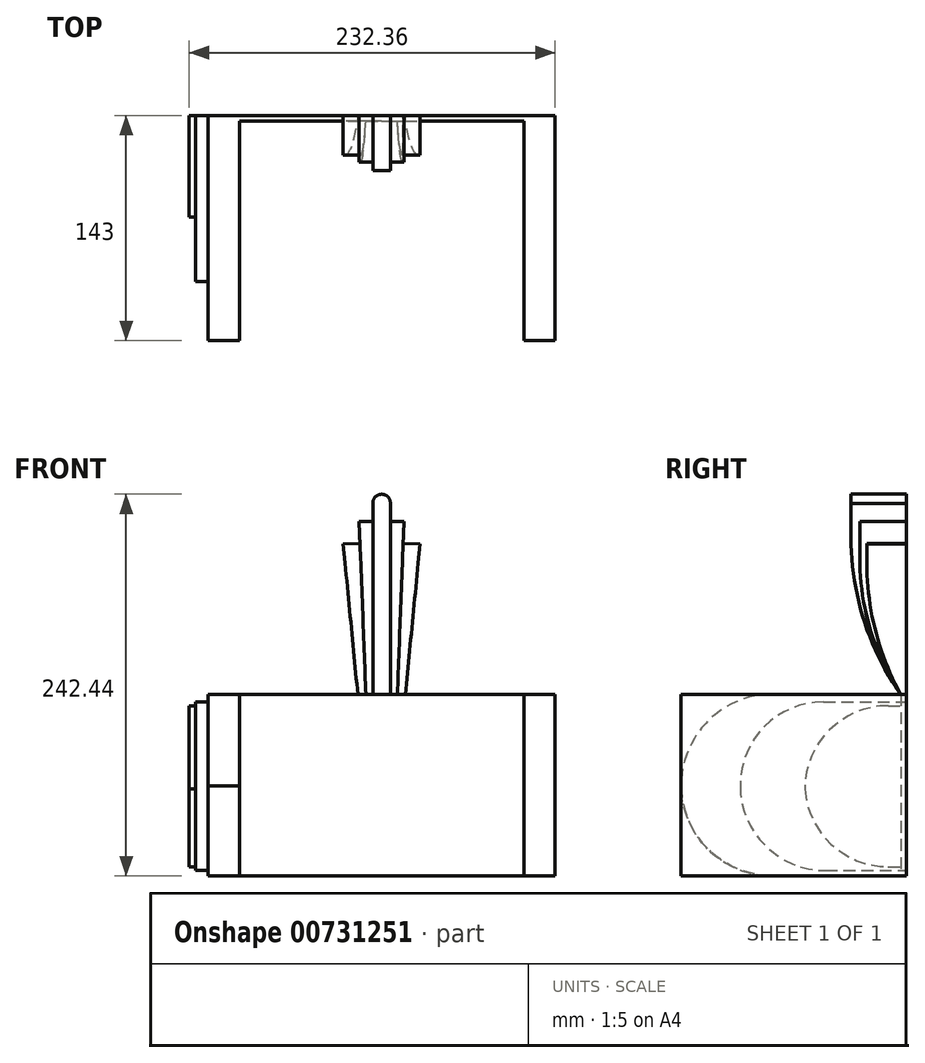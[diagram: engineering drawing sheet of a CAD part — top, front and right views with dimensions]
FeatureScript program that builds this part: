
annotation { "Feature Type Name" : "Feature", "Feature Type Description" : "" }
export const myFeature = defineFeature(function(context is Context, id is Id, definition is map)
    precondition{}
    {
        {
            var Q0;
            Q0=qCreatedBy(makeId("Front.planeOp"),FACE);
            var sketch = newSketch(context, id + "F0", { "sketchPlane" : qUnion([Q0])});
            skLineSegment(sketch, "E0", {"start": v(-110.18, 68.36) * mm, "end": v(-110.18, -47.05) * mm});
            skLineSegment(sketch, "E1", {"start": v(-110.18, -47.05) * mm, "end": v(110.18, -47.05) * mm});
            skLineSegment(sketch, "E2", {"start": v(0, 68.25) * mm, "end": v(-110.18, 68.36) * mm});
            skLineSegment(sketch, "E3", {"start": v(-90.36, 68.34) * mm, "end": v(-90.36, -47.05) * mm});
            skLineSegment(sketch, "E4", {"start": v(-110.18, 63.48) * mm, "end": v(-118.21, 63.48) * mm});
            skLineSegment(sketch, "E5", {"start": v(-118.21, 63.48) * mm, "end": v(-118.21, -43.66) * mm});
            skLineSegment(sketch, "E6", {"start": v(-118.21, -43.66) * mm, "end": v(-110.18, -43.66) * mm});
            skLineSegment(sketch, "E7", {"start": v(-118.21, 61.06) * mm, "end": v(-122.18, 61.06) * mm});
            skLineSegment(sketch, "E8", {"start": v(-122.18, 61.06) * mm, "end": v(-122.18, -41.16) * mm});
            skLineSegment(sketch, "E9", {"start": v(-122.18, -41.16) * mm, "end": v(-118.21, -41.16) * mm});
            skLineSegment(sketch, "E10", {"start": v(-5.61, 189.84) * mm, "end": v(-5.61, 68.26) * mm});
            skLineSegment(sketch, "E11", {"start": v(-5.61, 68.26) * mm, "end": v(0, 68.25) * mm});
            skLineSegment(sketch, "E12", {"start": v(-5.61, 178.11) * mm, "end": v(-14.22, 178.11) * mm});
            skLineSegment(sketch, "E13", {"start": v(-14.22, 178.11) * mm, "end": v(-10, 68.26) * mm});
            skLineSegment(sketch, "E14", {"start": v(-13.69, 164.25) * mm, "end": v(-24.38, 163.84) * mm});
            skLineSegment(sketch, "E15", {"start": v(-24.38, 163.84) * mm, "end": v(-15.12, 68.26) * mm});
            skLineSegment(sketch, "E16.MirrorCS", {"start": v(5.53, 189.84) * mm, "end": v(5.53, 68.26) * mm});
            skLineSegment(sketch, "E17.MirrorCS", {"start": v(5.53, 178.11) * mm, "end": v(14.22, 178.11) * mm});
            skLineSegment(sketch, "E18.MirrorCS", {"start": v(14.22, 178.11) * mm, "end": v(10, 68.26) * mm});
            skLineSegment(sketch, "E19.MirrorCS", {"start": v(13.69, 164.25) * mm, "end": v(24.38, 163.84) * mm});
            skLineSegment(sketch, "E20.MirrorCS", {"start": v(24.38, 163.84) * mm, "end": v(15.12, 68.26) * mm});
            skArc(sketch, "E21", {"start": v(5.53, 189.39) * mm, "mid": v(0.22, 195.38) * mm, "end": v(-5.55, 189.84) * mm});
            skLineSegment(sketch, "E22", {"start": v(-5.61, 189.84) * mm, "end": v(-5.55, 189.84) * mm});
            skLineSegment(sketch, "E23.MirrorCS", {"start": v(0, 68.25) * mm, "end": v(110.18, 68.36) * mm});
            skLineSegment(sketch, "E24.MirrorCS", {"start": v(90.36, 68.34) * mm, "end": v(90.36, -47.05) * mm});
            skLineSegment(sketch, "E25.MirrorCS", {"start": v(110.18, 68.36) * mm, "end": v(110.18, -47.05) * mm});
            skLineSegment(sketch, "E26.MirrorCS", {"start": v(110.18, 63.48) * mm, "end": v(118.21, 63.48) * mm});
            skLineSegment(sketch, "E27.MirrorCS", {"start": v(118.21, 63.48) * mm, "end": v(118.21, -43.66) * mm});
            skLineSegment(sketch, "E28.MirrorCS", {"start": v(122.18, 61.06) * mm, "end": v(122.18, -41.16) * mm});
            skLineSegment(sketch, "E29.MirrorCS", {"start": v(118.21, 61.06) * mm, "end": v(122.18, 61.06) * mm});
            skLineSegment(sketch, "E30.MirrorCS", {"start": v(118.21, -43.66) * mm, "end": v(110.18, -43.66) * mm});
            skLineSegment(sketch, "E31.MirrorCS", {"start": v(122.18, -41.16) * mm, "end": v(118.21, -41.16) * mm});
            skSolve(sketch);
        }
        {
            var Q0;
            {var subQ3=sQuery(id+"F0.wireOp",EDGE,"E3");Q0=makeQuery(id+"F0.imprint","IMPRINT",FACE,{"disambiguationData":[TD([[makeQuery(id+"F0.imprint","IMPRINT",EDGE,{"derivedFrom":subQ3}),-1.0]])]});}
            extrude(context, id + "F1", {"entities" : qUnion([Q0]), "depth" : 143 * mm, "offsetDistance" : 25 * mm});
        }
        {
            var Q0;
            {var subQ5=sQuery(id+"F0.wireOp",EDGE,"E3");Q0=makeQuery(id+"F0.imprint","IMPRINT",FACE,{"disambiguationData":[TD([[makeQuery(id+"F0.imprint","IMPRINT",EDGE,{"derivedFrom":subQ5}),1.0]])]});}
            extrude(context, id + "F2", {"entities" : qUnion([Q0]), "operationType" : NewBodyOperationType.ADD, "depth" : 3.5 * mm, "offsetDistance" : 25 * mm});
        }
        {
            var Q0;
            Q0=makeQuery(id+"F1.opExtrude","CAP_EDGE",EDGE,{"disambiguationData":[OSD([sQuery(id+"F0.wireOp",EDGE,"E2")])],"isStart":false});
            fillet(context, id + "F3", {"entities" : qUnion([Q0]), "radius" : 58.18 * mm, "tangentPropagation" : true, "allowEdgeOverflow" : false});
        }
        {
            var Q0;
            Q0=makeQuery(id+"F1.opExtrude","CAP_EDGE",EDGE,{"disambiguationData":[OSD([sQuery(id+"F0.wireOp",EDGE,"E1")])],"isStart":false});
            fillet(context, id + "F4", {"entities" : qUnion([Q0]), "radius" : 58.18 * mm, "tangentPropagation" : true, "allowEdgeOverflow" : false});
        }
        {
            var Q0;
            {var subQ4=sQuery(id+"F0.wireOp",EDGE,"E14");Q0=makeQuery(id+"F0.imprint","IMPRINT",FACE,{"disambiguationData":[TD([[makeQuery(id+"F0.imprint","IMPRINT",EDGE,{"derivedFrom":subQ4}),1.0]])]});}
            extrude(context, id + "F5", {"entities" : qUnion([Q0]), "operationType" : NewBodyOperationType.ADD, "depth" : 25 * mm, "offsetDistance" : 25 * mm});
        }
        {
            var Q0;
            {var subQ4=sQuery(id+"F0.wireOp",EDGE,"E12");Q0=makeQuery(id+"F0.imprint","IMPRINT",FACE,{"disambiguationData":[TD([[makeQuery(id+"F0.imprint","IMPRINT",EDGE,{"derivedFrom":subQ4}),1.0]])]});}
            extrude(context, id + "F6", {"entities" : qUnion([Q0]), "operationType" : NewBodyOperationType.ADD, "depth" : 29.5 * mm, "offsetDistance" : 25 * mm});
        }
        {
            var Q0;
            {var subQ4=sQuery(id+"F0.wireOp",EDGE,"E4");Q0=makeQuery(id+"F0.imprint","IMPRINT",FACE,{"disambiguationData":[TD([[makeQuery(id+"F0.imprint","IMPRINT",EDGE,{"derivedFrom":subQ4}),1.0]])]});}
            extrude(context, id + "F7", {"entities" : qUnion([Q0]), "operationType" : NewBodyOperationType.ADD, "depth" : 105.4 * mm, "offsetDistance" : 25 * mm});
        }
        {
            var Q0;
            {var subQ0=sQuery(id+"F0.wireOp",EDGE,"E7");Q0=makeQuery(id+"F0.imprint","IMPRINT",FACE,{"disambiguationData":[TD([[makeQuery(id+"F0.imprint","IMPRINT",EDGE,{"derivedFrom":subQ0}),1.0]])]});}
            extrude(context, id + "F8", {"entities" : qUnion([Q0]), "operationType" : NewBodyOperationType.ADD, "depth" : 64.3 * mm, "offsetDistance" : 25 * mm});
        }
        {
            var Q0;
            Q0=makeQuery(id+"F7.opExtrude","CAP_EDGE",EDGE,{"disambiguationData":[OSD([sQuery(id+"F0.wireOp",EDGE,"E4")])],"isStart":false});
            fillet(context, id + "F9", {"entities" : qUnion([Q0]), "radius" : 52.87 * mm, "tangentPropagation" : true, "allowEdgeOverflow" : false});
        }
        {
            var Q0;
            Q0=makeQuery(id+"F7.opExtrude","CAP_EDGE",EDGE,{"disambiguationData":[OSD([sQuery(id+"F0.wireOp",EDGE,"E6")])],"isStart":false});
            fillet(context, id + "F10", {"entities" : qUnion([Q0]), "radius" : 54.08 * mm, "tangentPropagation" : true, "allowEdgeOverflow" : false});
        }
        {
            var Q0;
            Q0=makeQuery(id+"F8.opExtrude","CAP_EDGE",EDGE,{"disambiguationData":[OSD([sQuery(id+"F0.wireOp",EDGE,"E7")])],"isStart":false});
            fillet(context, id + "F11", {"entities" : qUnion([Q0]), "radius" : 52.87 * mm, "tangentPropagation" : true, "allowEdgeOverflow" : false});
        }
        {
            var Q0;
            Q0=makeQuery(id+"F8.opExtrude","CAP_EDGE",EDGE,{"disambiguationData":[OSD([sQuery(id+"F0.wireOp",EDGE,"E9")])],"isStart":false});
            fillet(context, id + "F12", {"entities" : qUnion([Q0]), "radius" : 52.87 * mm, "tangentPropagation" : true, "allowEdgeOverflow" : false});
        }
        {
            var Q0;
            {var subQ0=sQuery(id+"F0.wireOp",EDGE,"E24.MirrorCS");Q0=makeQuery(id+"F0.imprint","IMPRINT",FACE,{"disambiguationData":[TD([[makeQuery(id+"F0.imprint","IMPRINT",EDGE,{"derivedFrom":subQ0}),1.0]])]});}
            extrude(context, id + "F13", {"entities" : qUnion([Q0]), "operationType" : NewBodyOperationType.ADD, "depth" : 143 * mm, "offsetDistance" : 25 * mm});
        }
        {
            var Q0;
            {var subQ10=sQuery(id+"F0.wireOp",EDGE,"E21");Q0=makeQuery(id+"F0.imprint","IMPRINT",FACE,{"disambiguationData":[TD([[makeQuery(id+"F0.imprint","IMPRINT",EDGE,{"derivedFrom":subQ10}),1.0]])]});}
            extrude(context, id + "F14", {"entities" : qUnion([Q0]), "operationType" : NewBodyOperationType.ADD, "depth" : 35 * mm, "offsetDistance" : 25 * mm});
        }
        {
            var Q0;
            {var subQ0=sQuery(id+"F0.wireOp",EDGE,"E19.MirrorCS");Q0=makeQuery(id+"F0.imprint","IMPRINT",FACE,{"disambiguationData":[TD([[makeQuery(id+"F0.imprint","IMPRINT",EDGE,{"derivedFrom":subQ0}),-1.0]])]});}
            extrude(context, id + "F15", {"entities" : qUnion([Q0]), "operationType" : NewBodyOperationType.ADD, "depth" : 25 * mm, "offsetDistance" : 25 * mm});
        }
        {
            var Q0;
            {var subQ1=sQuery(id+"F0.wireOp",EDGE,"E17.MirrorCS");Q0=makeQuery(id+"F0.imprint","IMPRINT",FACE,{"disambiguationData":[TD([[makeQuery(id+"F0.imprint","IMPRINT",EDGE,{"derivedFrom":subQ1}),-1.0]])]});}
            extrude(context, id + "F16", {"entities" : qUnion([Q0]), "operationType" : NewBodyOperationType.ADD, "depth" : 29.5 * mm, "offsetDistance" : 25 * mm});
        }
        {
            var Q0;
            Q0=makeQuery(id+"F5.opExtrude","CAP_EDGE",EDGE,{"disambiguationData":[OSD([sQuery(id+"F0.wireOp",EDGE,"E2")])],"isStart":false});
            fillet(context, id + "F17", {"entities" : qUnion([Q0]), "radius" : 172.62 * mm, "tangentPropagation" : true, "allowEdgeOverflow" : false});
        }
        {
            var Q0;
            Q0=makeQuery(id+"F15.opExtrude","CAP_EDGE",EDGE,{"disambiguationData":[OSD([sQuery(id+"F0.wireOp",EDGE,"E23.MirrorCS")])],"isStart":false});
            fillet(context, id + "F18", {"entities" : qUnion([Q0]), "radius" : 172.62 * mm, "tangentPropagation" : true, "allowEdgeOverflow" : false});
        }
        {
            var Q0;
            Q0=makeQuery(id+"F16.opExtrude","CAP_EDGE",EDGE,{"disambiguationData":[OSD([sQuery(id+"F0.wireOp",EDGE,"E23.MirrorCS")])],"isStart":false});
            fillet(context, id + "F19", {"entities" : qUnion([Q0]), "radius" : 157.65 * mm, "tangentPropagation" : true, "allowEdgeOverflow" : false});
        }
        {
            var Q0;
            Q0=makeQuery(id+"F6.opExtrude","CAP_EDGE",EDGE,{"disambiguationData":[OSD([sQuery(id+"F0.wireOp",EDGE,"E2")])],"isStart":false});
            fillet(context, id + "F20", {"entities" : qUnion([Q0]), "radius" : 157.65 * mm, "tangentPropagation" : true, "allowEdgeOverflow" : false});
        }
        {
            var Q0;
            Q0=makeQuery(id+"F14.opExtrude","CAP_EDGE",EDGE,{"disambiguationData":[OSD([sQuery(id+"F0.wireOp",EDGE,"E23.MirrorCS")])],"isStart":false});
            fillet(context, id + "F21", {"entities" : qUnion([Q0]), "radius" : 173.82 * mm, "tangentPropagation" : true, "allowEdgeOverflow" : false});
        }
    });
